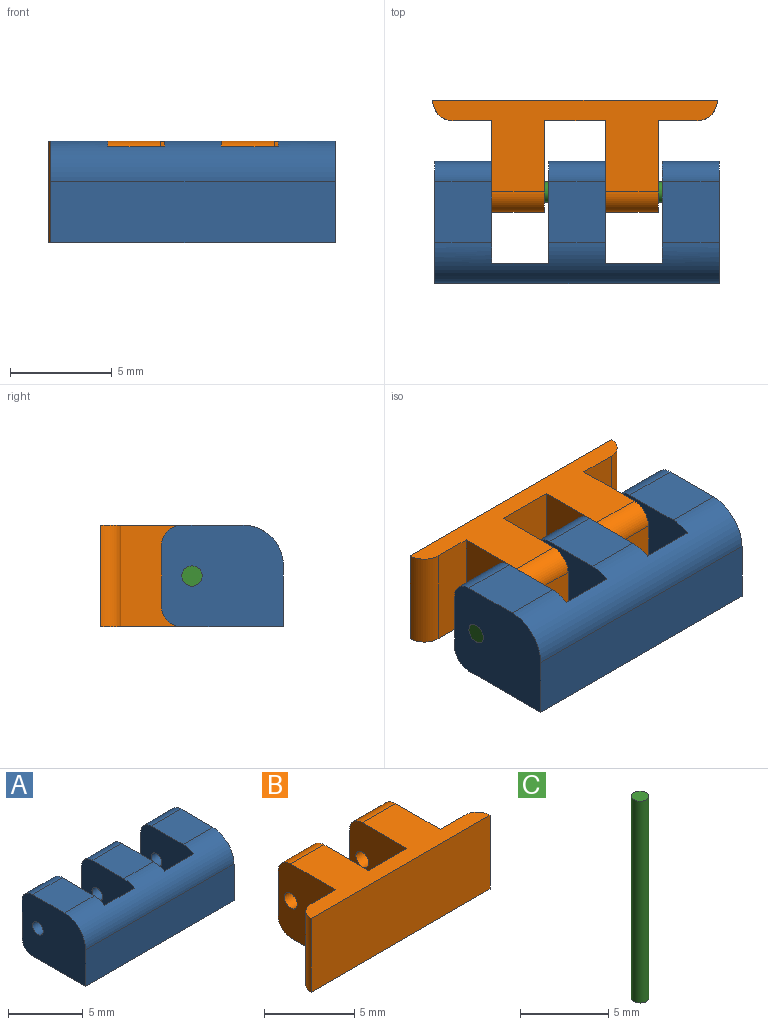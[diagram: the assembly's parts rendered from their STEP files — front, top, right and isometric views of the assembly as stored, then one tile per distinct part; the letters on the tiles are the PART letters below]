
ASSEMBLY  parts=3 mates=2
PART A: 26 faces, bbox 14x6x5 mm
  f0: plane 3x2.8mm, normal (0,0,1), area 8.4mm2, adj f11,f13,f19,f25
  f1: plane 3x2.8mm, normal (0,0,1), area 8.4mm2, adj f7,f9,f20,f25
  f2: plane 14x3mm, normal (0,-1,0), area 42mm2, adj f3,f13,f15,f25
  f3: plane 6x5mm, normal (1,0,0), area 27.9mm2, adj f2,f4,f14,f15,f18,f21,f24,f25
  f4: plane 3x2.8mm, normal (0,1,0), area 8.4mm2, adj f3,f5,f18,f21
  f5: plane 5x5mm, normal (-1,0,0), area 23.7mm2, adj f4,f6,f14,f15,f18,f21,f24,f25
  f6: plane 4.73x2.8mm, normal (0,1,0), area 13.2mm2, adj f5,f7,f15,f25
  f7: plane 5x5mm, normal (1,0,0), area 23.7mm2, adj f1,f6,f8,f15,f17,f20,f23,f25
  f8: plane 3x2.8mm, normal (0,1,0), area 8.4mm2, adj f7,f9,f17,f20
  f9: plane 5x5mm, normal (-1,0,0), area 23.7mm2, adj f1,f8,f10,f15,f17,f20,f23,f25
  f10: plane 4.73x2.8mm, normal (0,1,0), area 13.2mm2, adj f9,f11,f15,f25
  f11: plane 5x5mm, normal (1,0,0), area 23.7mm2, adj f0,f10,f12,f15,f16,f19,f22,f25
  f12: plane 3x2.8mm, normal (0,1,0), area 8.4mm2, adj f11,f13,f16,f19
  f13: plane 6x5mm, normal (-1,0,0), area 27.9mm2, adj f0,f2,f12,f15,f16,f19,f22,f25
  f14: plane 3x2.8mm, normal (0,0,1), area 8.4mm2, adj f3,f5,f21,f25
  f15: plane 14x5mm, normal (0,0,-1), area 47.6mm2, adj f2,f3,f5,f6,f7,f9,f10,f11
  f16: cylinder r=1mm len=2.8mm, axis (-1,0,0), area 4.4mm2, adj f11,f12,f13,f15
  f17: cylinder r=1mm len=2.8mm, axis (-1,0,0), area 4.4mm2, adj f7,f8,f9,f15
  f18: cylinder r=1mm len=2.8mm, axis (-1,0,0), area 4.4mm2, adj f3,f4,f5,f15
  f19: cylinder r=1mm len=2.8mm, axis (1,0,0), area 4.4mm2, adj f0,f11,f12,f13
  f20: cylinder r=1mm len=2.8mm, axis (1,0,0), area 4.4mm2, adj f1,f7,f8,f9
  f21: cylinder r=1mm len=2.8mm, axis (1,0,0), area 4.4mm2, adj f3,f4,f5,f14
  f22: cylinder r=0.5mm len=2.8mm, axis (1,0,0), area 8.8mm2, adj f11,f13
  f23: cylinder r=0.5mm len=2.8mm, axis (1,0,0), area 8.8mm2, adj f7,f9
  f24: cylinder r=0.5mm len=2.8mm, axis (1,0,0), area 8.8mm2, adj f3,f5
  f25: cylinder r=2mm len=14mm, axis (-1,0,0), area 38.1mm2, adj f0,f1,f2,f3,f5,f6,f7,f9
PART B: 20 faces, bbox 14x5.5x5 mm
  f0: plane 5x3mm, normal (0,1,0), area 15mm2, adj f1,f9,f10,f11
  f1: plane 5x4.5mm, normal (1,0,0), area 21.3mm2, adj f0,f2,f10,f11,f13,f17,f19
  f2: plane 3x2.6mm, normal (0,1,0), area 7.8mm2, adj f1,f3,f17,f19
  f3: plane 5x4.5mm, normal (-1,0,0), area 21.3mm2, adj f2,f4,f10,f11,f13,f17,f19
  f4: plane 5x1.9mm, normal (0,1,0), area 9.5mm2, adj f3,f10,f11,f14
  f5: plane 14x5mm, normal (0,-1,0), area 70mm2, adj f10,f11,f14,f15
  f6: plane 5x1.9mm, normal (0,1,0), area 9.5mm2, adj f7,f10,f11,f15
  f7: plane 5x4.5mm, normal (1,0,0), area 21.3mm2, adj f6,f8,f10,f11,f12,f16,f18
  f8: plane 3x2.6mm, normal (0,1,0), area 7.8mm2, adj f7,f9,f16,f18
  f9: plane 5x4.5mm, normal (-1,0,0), area 21.3mm2, adj f0,f8,f10,f11,f12,f16,f18
  f10: plane 14x4.5mm, normal (0,0,1), area 31.8mm2, adj f0,f1,f3,f4,f5,f6,f7,f9
  f11: plane 14x4.5mm, normal (0,0,-1), area 31.8mm2, adj f0,f1,f3,f4,f5,f6,f7,f9
  f12: cylinder r=0.5mm len=2.6mm, axis (1,0,0), area 8.2mm2, adj f7,f9
  f13: cylinder r=0.5mm len=2.6mm, axis (1,0,0), area 8.2mm2, adj f1,f3
  f14: cylinder r=1mm len=5mm, axis (0,0,1), area 7.9mm2, adj f4,f5,f10,f11
  f15: cylinder r=1mm len=5mm, axis (0,0,-1), area 7.9mm2, adj f5,f6,f10,f11
  f16: cylinder r=1mm len=2.6mm, axis (-1,0,0), area 4.1mm2, adj f7,f8,f9,f11
  f17: cylinder r=1mm len=2.6mm, axis (-1,0,0), area 4.1mm2, adj f1,f2,f3,f11
  f18: cylinder r=1mm len=2.6mm, axis (1,0,0), area 4.1mm2, adj f7,f8,f9,f10
  f19: cylinder r=1mm len=2.6mm, axis (1,0,0), area 4.1mm2, adj f1,f2,f3,f10
PART C: 3 faces, bbox 1x1x14 mm
  f0: cylinder r=0.5mm len=14mm, axis (0,0,-1), area 44mm2, adj f1,f2
  f1: plane 1x1mm, normal (0,0,1), area 0.8mm2, adj f0
  f2: plane 1x1mm, normal (0,0,-1), area 0.8mm2, adj f0
PLACE A t=(-3.57,-5.73,-3.15)mm
PLACE B rot(axis=(0,0,1),180deg) t=(-4.65,2.77,-3.15)mm
PLACE C rot(axis=(0,1,0),90deg) t=(-11.55,-1.23,-0.65)mm
MATE revolute B.f12 <-> A.f22  axis (-1,0,0) through (-8.75,-1.23,-0.65)mm
MATE revolute C.f0 <-> A.f22  axis (1,0,0) through (2.45,-1.23,-0.65)mm
